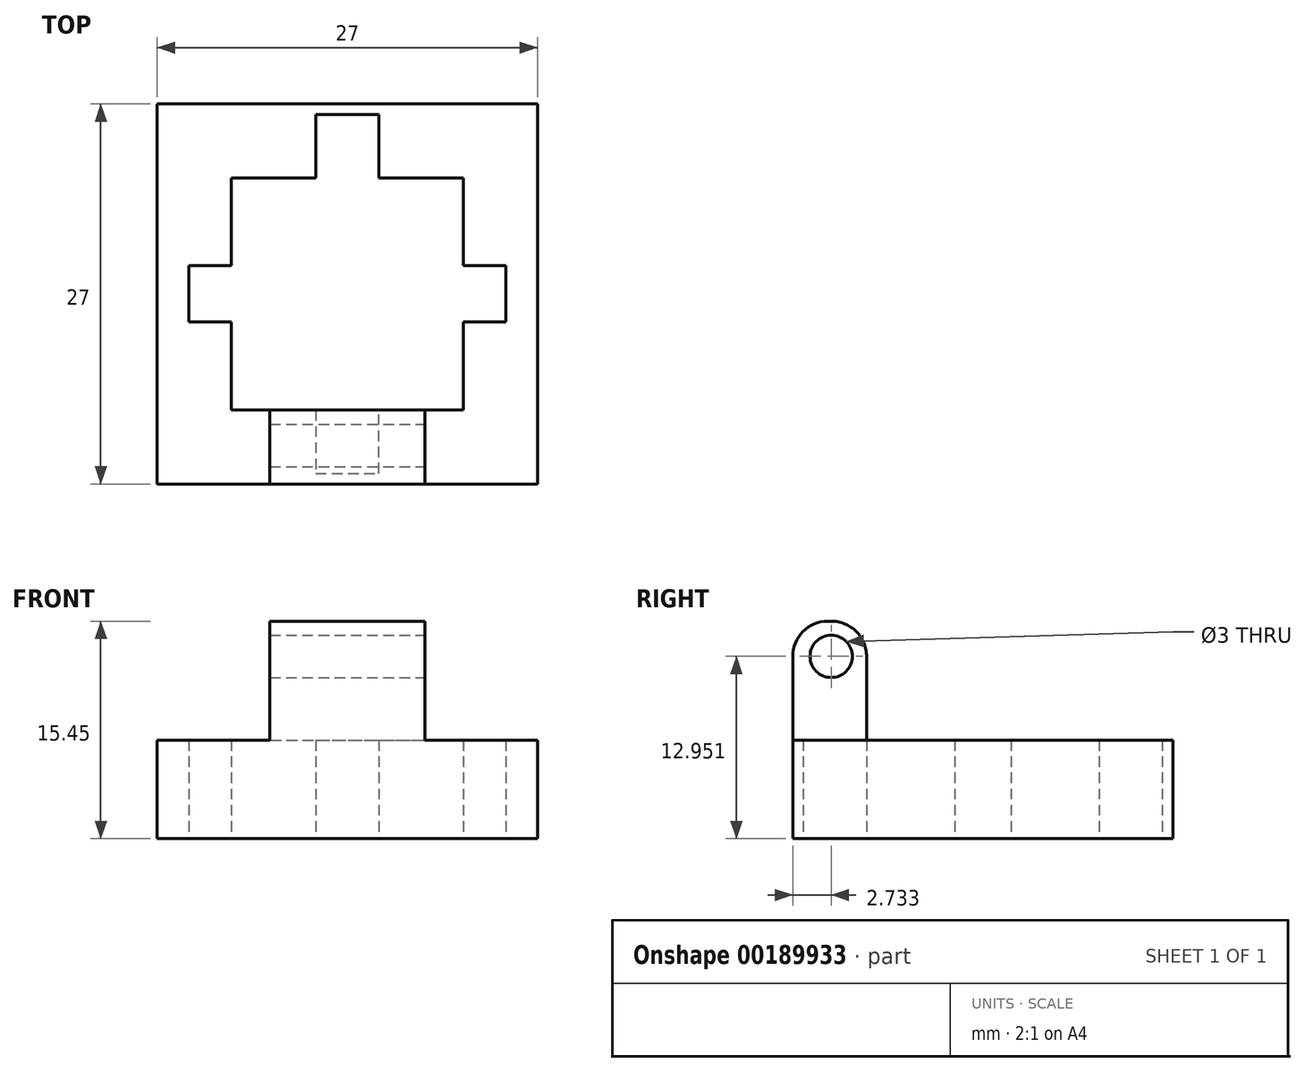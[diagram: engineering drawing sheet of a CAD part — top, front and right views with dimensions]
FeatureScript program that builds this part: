
annotation { "Feature Type Name" : "Feature", "Feature Type Description" : "" }
export const myFeature = defineFeature(function(context is Context, id is Id, definition is map)
    precondition{}
    {
        {
            var Q0;
            Q0=qCreatedBy(makeId("Top.planeOp"),FACE);
            var sketch = newSketch(context, id + "F0", { "sketchPlane" : qUnion([Q0])});
            skLineSegment(sketch, "E0.bottom", {"start": v(-8.25, 8.25) * mm, "end": v(-2.25, 8.25) * mm});
            skLineSegment(sketch, "E0.top", {"start": v(-8.25, -8.25) * mm, "end": v(-2.25, -8.25) * mm});
            skLineSegment(sketch, "E0.left", {"start": v(-8.25, 8.25) * mm, "end": v(-8.25, 2) * mm});
            skLineSegment(sketch, "E0.right", {"start": v(8.25, 8.25) * mm, "end": v(8.25, 2) * mm});
            skLineSegment(sketch, "E1.bottom", {"start": v(-13.5, 13.5) * mm, "end": v(13.5, 13.5) * mm});
            skLineSegment(sketch, "E1.top", {"start": v(-13.5, -13.5) * mm, "end": v(13.5, -13.5) * mm});
            skLineSegment(sketch, "E1.left", {"start": v(-13.5, 13.5) * mm, "end": v(-13.5, -13.5) * mm});
            skLineSegment(sketch, "E1.right", {"start": v(13.5, 13.5) * mm, "end": v(13.5, -13.5) * mm});
            skLineSegment(sketch, "E2", {"start": v(-2.25, 8.25) * mm, "end": v(-2.25, 12.75) * mm});
            skLineSegment(sketch, "E3", {"start": v(-2.25, 12.75) * mm, "end": v(2.25, 12.75) * mm});
            skLineSegment(sketch, "E4", {"start": v(2.25, 12.75) * mm, "end": v(2.25, 8.25) * mm});
            skLineSegment(sketch, "E5", {"start": v(-2.25, -8.25) * mm, "end": v(-2.25, -12.75) * mm});
            skLineSegment(sketch, "E6", {"start": v(-2.25, -12.75) * mm, "end": v(2.25, -12.75) * mm});
            skLineSegment(sketch, "E7", {"start": v(2.25, -12.75) * mm, "end": v(2.25, -8.25) * mm});
            skLineSegment(sketch, "E8", {"start": v(-8.25, -2) * mm, "end": v(-11.25, -2) * mm});
            skLineSegment(sketch, "E9", {"start": v(-11.25, -2) * mm, "end": v(-11.25, 2) * mm});
            skLineSegment(sketch, "E10", {"start": v(-11.25, 2) * mm, "end": v(-8.25, 2) * mm});
            skLineSegment(sketch, "E11", {"start": v(8.25, -2) * mm, "end": v(11.25, -2) * mm});
            skLineSegment(sketch, "E12", {"start": v(11.25, -2) * mm, "end": v(11.25, 2) * mm});
            skLineSegment(sketch, "E13", {"start": v(11.25, 2) * mm, "end": v(8.25, 2) * mm});
            skLineSegment(sketch, "E14.trimOffspring", {"start": v(2.25, 8.25) * mm, "end": v(8.25, 8.25) * mm});
            skLineSegment(sketch, "E15.trimOffspring", {"start": v(-8.25, -2) * mm, "end": v(-8.25, -8.25) * mm});
            skLineSegment(sketch, "E16.trimOffspring", {"start": v(8.25, -2) * mm, "end": v(8.25, -8.25) * mm});
            skLineSegment(sketch, "E17.trimOffspring", {"start": v(2.25, -8.25) * mm, "end": v(8.25, -8.25) * mm});
            skSolve(sketch);
        }
        {
            var Q0;
            Q0=makeQuery(id+"F0.imprint","IMPRINT",FACE,{"disambiguationData":[TD([[makeQuery(id+"F0.imprint","IMPRINT",EDGE,{"derivedFrom":sQuery(id+"F0.wireOp",EDGE,"E0.bottom")}),1.0]])]});
            extrude(context, id + "F1", {"entities" : qUnion([Q0]), "depth" : 7 * mm});
        }
        {
            var Q0;
            Q0=makeQuery(id+"F1.opExtrude","SWEPT_FACE",FACE,{"disambiguationData":[OSD([sQuery(id+"F0.wireOp",EDGE,"E1.right")])]});
            var sketch = newSketch(context, id + "F2", { "sketchPlane" : qUnion([Q0])});
            skLineSegment(sketch, "E18", {"start": v(-13.5, 7) * mm, "end": v(-13.5, 15.44) * mm});
            skPoint(sketch, "E19", {"position": v(-8.25, 7) * mm});
            skLineSegment(sketch, "E20", {"start": v(-8.25, 7) * mm, "end": v(-8.25, 15.46) * mm});
            skLineSegment(sketch, "E21", {"start": v(-8.25, 15.46) * mm, "end": v(-13.5, 15.44) * mm});
            skSolve(sketch);
        }
        {
            var Q0;
            {var subQ0=sQuery(id+"F2.wireOp",EDGE,"E18");Q0=makeQuery(id+"F2.imprint","IMPRINT",FACE,{"disambiguationData":[TD([[makeQuery(id+"F2.imprint","IMPRINT",EDGE,{"derivedFrom":subQ0}),-1.0]])]});}
            extrude(context, id + "F3", {"entities" : qUnion([Q0]), "operationType" : NewBodyOperationType.ADD, "oppositeDirection" : true, "depth" : 19 * mm, "hasSecondDirection" : true, "secondDirectionOppositeDirection" : true, "secondDirectionDepth" : 8 * mm});
        }
        {
            var Q0;
            Q0=makeQuery(id+"F3.opExtrude","SWEPT_EDGE",EDGE,{"disambiguationData":[OSD([sQuery(id+"F2.wireOp",EDGE,"E20"),sQuery(id+"F2.wireOp",EDGE,"E21")])]});
            var Q1;
            Q1=makeQuery(id+"F3.opExtrude","SWEPT_EDGE",EDGE,{"disambiguationData":[OSD([sQuery(id+"F2.wireOp",EDGE,"E18"),sQuery(id+"F2.wireOp",EDGE,"E21")])]});
            fillet(context, id + "F4", {"entities" : qUnion([Q0, Q1]), "radius" : 2.5 * mm, "tangentPropagation" : true, "allowEdgeOverflow" : false});
        }
        {
            var Q0;
            Q0=makeQuery(id+"F3.opExtrude","CAP_FACE",FACE,{"disambiguationData":[OSD([sQuery(id+"F0.wireOp",EDGE,"E1.right"),sQuery(id+"F2.wireOp",EDGE,"E18"),sQuery(id+"F2.wireOp",EDGE,"E20"),sQuery(id+"F2.wireOp",EDGE,"E21")])],"isStart":true});
            var sketch = newSketch(context, id + "F5", { "sketchPlane" : qUnion([Q0])});
            skLineSegment(sketch, "E22", {"start": v(-13.5, 12.95) * mm, "end": v(-8.25, 12.95) * mm, "construction": true});
            skPoint(sketch, "E23", {"position": v(-10.77, 12.95) * mm});
            skSolve(sketch);
        }
        {
            var Q0;
            Q0=sQuery(id+"F5.wireOp",VERTEX,"E23");
            var Q1;
            Q1=makeQuery(id+"F1.opExtrude","SWEPT_BODY",BODY,{"disambiguationData":[OSD([sQuery(id+"F0.wireOp",EDGE,"E0.bottom"),sQuery(id+"F0.wireOp",EDGE,"E0.top"),sQuery(id+"F0.wireOp",EDGE,"E0.left"),sQuery(id+"F0.wireOp",EDGE,"E0.right"),sQuery(id+"F0.wireOp",EDGE,"E1.bottom"),sQuery(id+"F0.wireOp",EDGE,"E1.top"),sQuery(id+"F0.wireOp",EDGE,"E1.left"),sQuery(id+"F0.wireOp",EDGE,"E1.right"),sQuery(id+"F0.wireOp",EDGE,"E2"),sQuery(id+"F0.wireOp",EDGE,"E3"),sQuery(id+"F0.wireOp",EDGE,"E4"),sQuery(id+"F0.wireOp",EDGE,"E5"),sQuery(id+"F0.wireOp",EDGE,"E6"),sQuery(id+"F0.wireOp",EDGE,"E7"),sQuery(id+"F0.wireOp",EDGE,"E8"),sQuery(id+"F0.wireOp",EDGE,"E9"),sQuery(id+"F0.wireOp",EDGE,"E10"),sQuery(id+"F0.wireOp",EDGE,"E11"),sQuery(id+"F0.wireOp",EDGE,"E12"),sQuery(id+"F0.wireOp",EDGE,"E13"),sQuery(id+"F0.wireOp",EDGE,"E14.trimOffspring"),sQuery(id+"F0.wireOp",EDGE,"E15.trimOffspring"),sQuery(id+"F0.wireOp",EDGE,"E16.trimOffspring"),sQuery(id+"F0.wireOp",EDGE,"E17.trimOffspring")])]});
            hole(context, id + "F6", {"style" : HoleStyle.SIMPLE, "endStyle" : HoleEndStyle.THROUGH, "holeDiameter" : 3 * mm, "locations" : qUnion([Q0]), "scope" : qUnion([Q1]), "isTappedThrough" : true});
        }
    });
